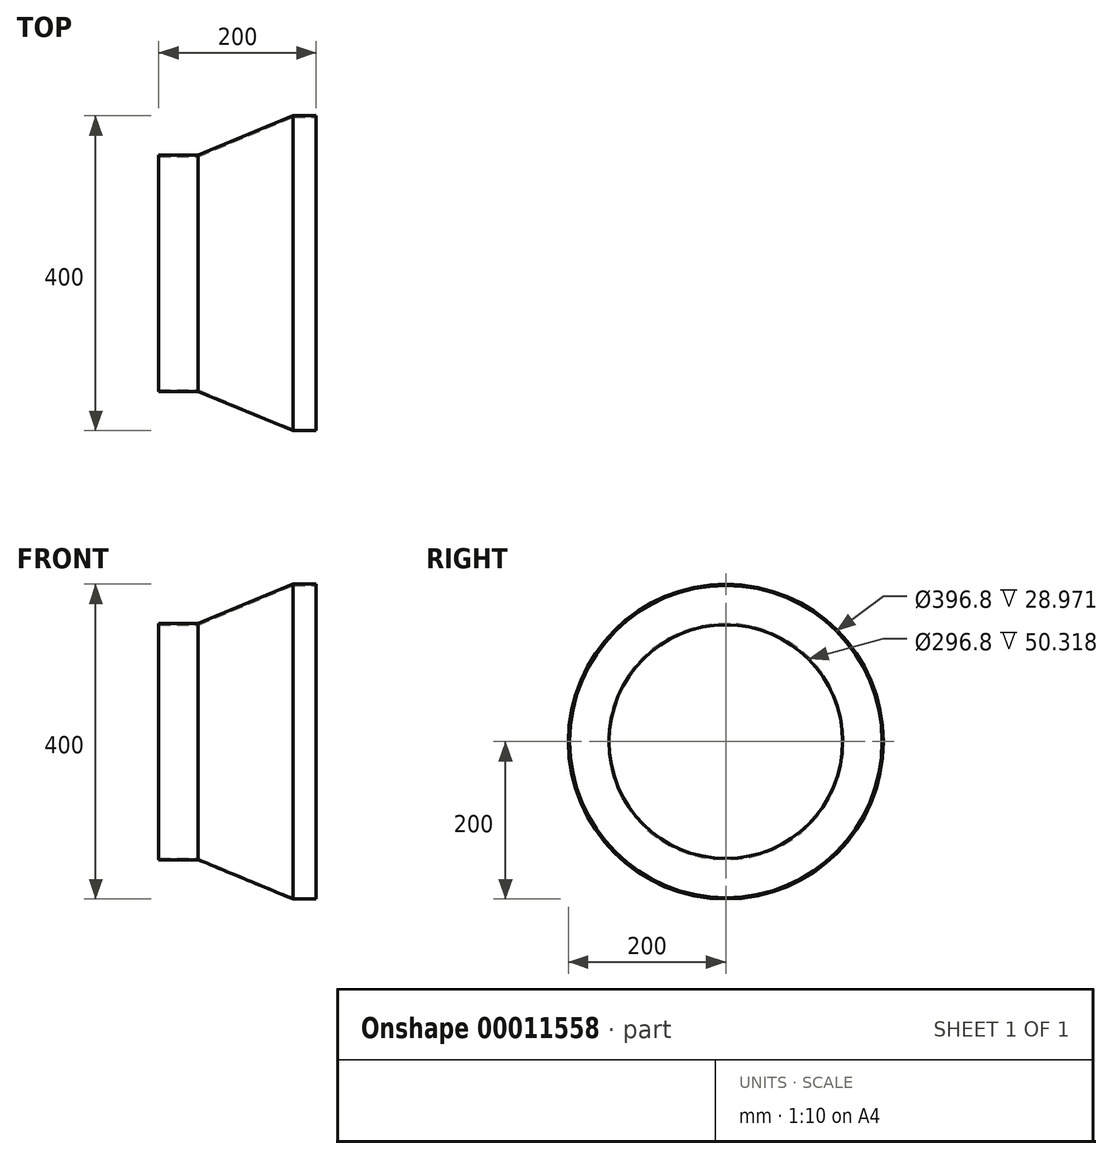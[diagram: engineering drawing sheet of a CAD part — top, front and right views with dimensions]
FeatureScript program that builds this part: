
annotation { "Feature Type Name" : "Feature", "Feature Type Description" : "" }
export const myFeature = defineFeature(function(context is Context, id is Id, definition is map)
    precondition{}
    {
        {
            var Q0;
            Q0=qCreatedBy(makeId("Right.planeOp"),FACE);
            var sketch = newSketch(context, id + "F0", { "sketchPlane" : qUnion([Q0])});
            skCircle(sketch, "E0", {"center": v(0, 0) * mm, "radius": 200 * mm});
            skSolve(sketch);
        }
        {
            var Q0;
            Q0 = qSketchRegion(id + "F0", true);
            extrude(context, id + "F1", {"entities" : qUnion([Q0]), "oppositeDirection" : true, "depth" : 150 * mm});
        }
        {
            var Q0;
            Q0=makeQuery(id+"F1.opExtrude","CAP_EDGE",EDGE,{"disambiguationData":[OSD([sQuery(id+"F0.wireOp",EDGE,"E0")])],"isStart":false});
            chamfer(context, id + "F2", {"entities" : qUnion([Q0]), "chamferType" : ChamferType.OFFSET_ANGLE, "width" : 50 * mm, "oppositeDirection" : true, "angle" : 67.5 * degree, "tangentPropagation" : true});
        }
        {
            var Q0;
            Q0=makeQuery(id+"F1.opExtrude","CAP_FACE",FACE,{"disambiguationData":[OSD([sQuery(id+"F0.wireOp",EDGE,"E0")])],"isStart":false});
            extrude(context, id + "F3", {"entities" : qUnion([Q0]), "operationType" : NewBodyOperationType.ADD, "depth" : 50 * mm});
        }
        {
            var Q0;
            Q0=makeQuery(id+"F3.opExtrude","CAP_FACE",FACE,{"disambiguationData":[OSD([sQuery(id+"F0.wireOp",EDGE,"E0")])],"isStart":false});
            var Q1;
            Q1=makeQuery(id+"F1.opExtrude","CAP_FACE",FACE,{"disambiguationData":[OSD([sQuery(id+"F0.wireOp",EDGE,"E0")])],"isStart":true});
            shell(context, id + "F4", {"entities" : qUnion([Q0, Q1]), "thickness" : 1.6 * mm});
        }
    });
